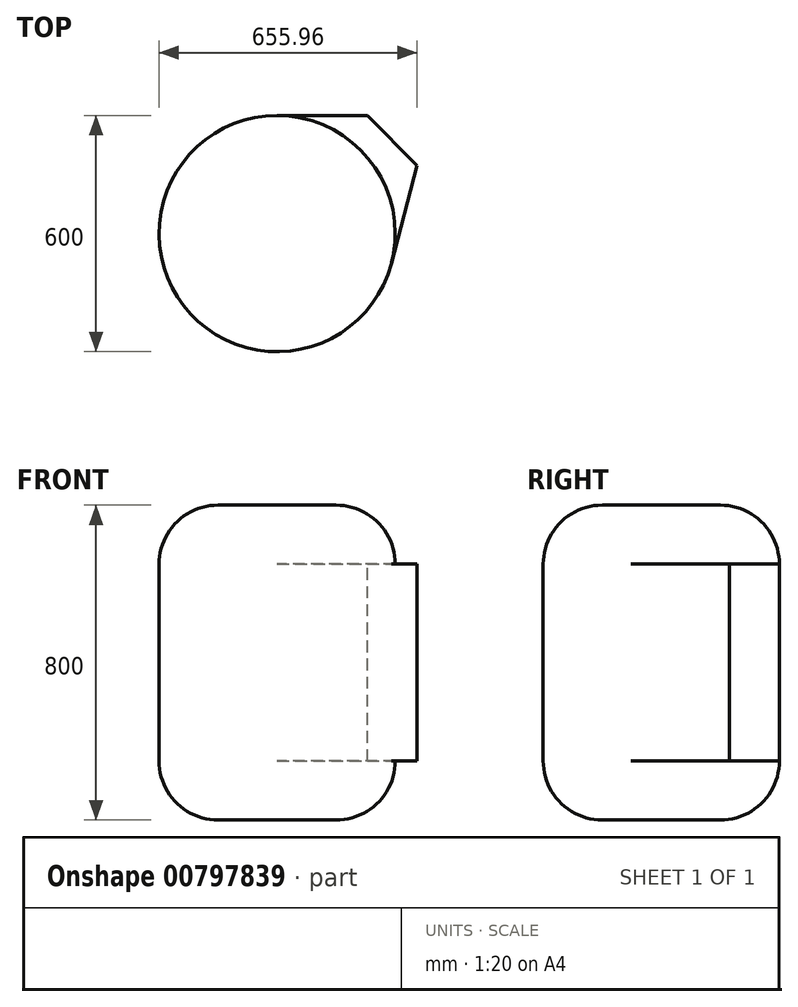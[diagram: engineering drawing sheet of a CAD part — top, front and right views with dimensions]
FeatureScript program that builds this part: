
annotation { "Feature Type Name" : "Feature", "Feature Type Description" : "" }
export const myFeature = defineFeature(function(context is Context, id is Id, definition is map)
    precondition{}
    {
        {
            var Q0;
            Q0=qCreatedBy(makeId("Top.planeOp"),FACE);
            var sketch = newSketch(context, id + "F0", { "sketchPlane" : qUnion([Q0])});
            skCircle(sketch, "E0", {"center": v(0, 0) * mm, "radius": 300 * mm});
            skSolve(sketch);
        }
        {
            var Q0;
            Q0 = qSketchRegion(id + "F0", true);
            extrude(context, id + "F1", {"entities" : qUnion([Q0]), "depth" : 800 * mm, "offsetDistance" : 25 * mm});
        }
        {
            var Q0;
            Q0=makeQuery(id+"F1.opExtrude","CAP_FACE",FACE,{"disambiguationData":[OSD([sQuery(id+"F0.wireOp",EDGE,"E0")])],"isStart":false});
            var Q1;
            Q1=makeQuery(id+"F1.opExtrude","CAP_EDGE",EDGE,{"disambiguationData":[OSD([sQuery(id+"F0.wireOp",EDGE,"E0")])],"isStart":true});
            fillet(context, id + "F2", {"entities" : qUnion([Q0, Q1]), "radius" : 150 * mm, "tangentPropagation" : true, "allowEdgeOverflow" : false});
        }
        {
            var Q0;
            Q0=makeQuery(id+"F1.opExtrude","CAP_FACE",FACE,{"disambiguationData":[OSD([sQuery(id+"F0.wireOp",EDGE,"E0")])],"isStart":false});
            var sketch = newSketch(context, id + "F3", { "sketchPlane" : qUnion([Q0])});
            skLineSegment(sketch, "E1.bottom", {"start": v(0, 0) * mm, "end": v(300, 0) * mm});
            skLineSegment(sketch, "E1.top", {"start": v(0, 300) * mm, "end": v(300, 300) * mm});
            skLineSegment(sketch, "E1.left", {"start": v(0, 0) * mm, "end": v(0, 300) * mm});
            skLineSegment(sketch, "E1.right", {"start": v(300, 0) * mm, "end": v(300, 300) * mm});
            skLineSegment(sketch, "E2", {"start": v(0, 0) * mm, "end": v(300, 300) * mm});
            skLineSegment(sketch, "E3", {"start": v(300, 300) * mm, "end": v(370.71, 229.29) * mm});
            skCircle(sketch, "E4", {"center": v(0, 0) * mm, "radius": 300 * mm});
            skLineSegment(sketch, "E5", {"start": v(370.71, 229.29) * mm, "end": v(290.09, -76.49) * mm});
            skLineSegment(sketch, "E6", {"start": v(0, 0) * mm, "end": v(290.09, -76.49) * mm});
            skLineSegment(sketch, "E7.0", {"start": v(229.29, 300) * mm, "end": v(355.96, 173.33) * mm});
            skSolve(sketch);
        }
        {
            var Q0;
            {var subQ0=sQuery(id+"F3.wireOp",EDGE,"E4");var subQ5=sQuery(id+"F3.wireOp",EDGE,"E2");var subQ6=makeQuery(id+"F3.imprint","INTERSECT",VERTEX,{"derivedFrom":[subQ5,subQ0]});Q0=makeQuery(id+"F3.imprint","IMPRINT",FACE,{"disambiguationData":[TD([[makeQuery(id+"F3.imprint","IMPRINT",EDGE,{"disambiguationData":[TD([[subQ6,-1.0]])],"derivedFrom":subQ5}),1.0]])]});}
            var Q1;
            {var subQ0=sQuery(id+"F3.wireOp",EDGE,"E4");var subQ5=sQuery(id+"F3.wireOp",EDGE,"E2");var subQ6=makeQuery(id+"F3.imprint","INTERSECT",VERTEX,{"derivedFrom":[subQ5,subQ0]});Q1=makeQuery(id+"F3.imprint","IMPRINT",FACE,{"disambiguationData":[TD([[makeQuery(id+"F3.imprint","IMPRINT",EDGE,{"disambiguationData":[TD([[subQ6,-1.0]])],"derivedFrom":subQ5}),-1.0]])]});}
            var Q2;
            {var subQ3=sQuery(id+"F3.wireOp",EDGE,"E7.0");var subQ5=sQuery(id+"F3.wireOp",EDGE,"E5");var subQ7=makeQuery(id+"F3.imprint","INTERSECT",VERTEX,{"derivedFrom":[subQ5,subQ3]});Q2=makeQuery(id+"F3.imprint","IMPRINT",FACE,{"disambiguationData":[TD([[makeQuery(id+"F3.imprint","IMPRINT",EDGE,{"disambiguationData":[TD([[subQ7,1.0]])],"derivedFrom":subQ3}),-1.0]])]});}
            extrude(context, id + "F4", {"entities" : qUnion([Q0, Q1, Q2]), "operationType" : NewBodyOperationType.ADD, "oppositeDirection" : true, "depth" : 650 * mm, "offsetDistance" : 25 * mm, "hasSecondDirection" : true, "secondDirectionOppositeDirection" : true, "secondDirectionDepth" : 150 * mm});
        }
    });
